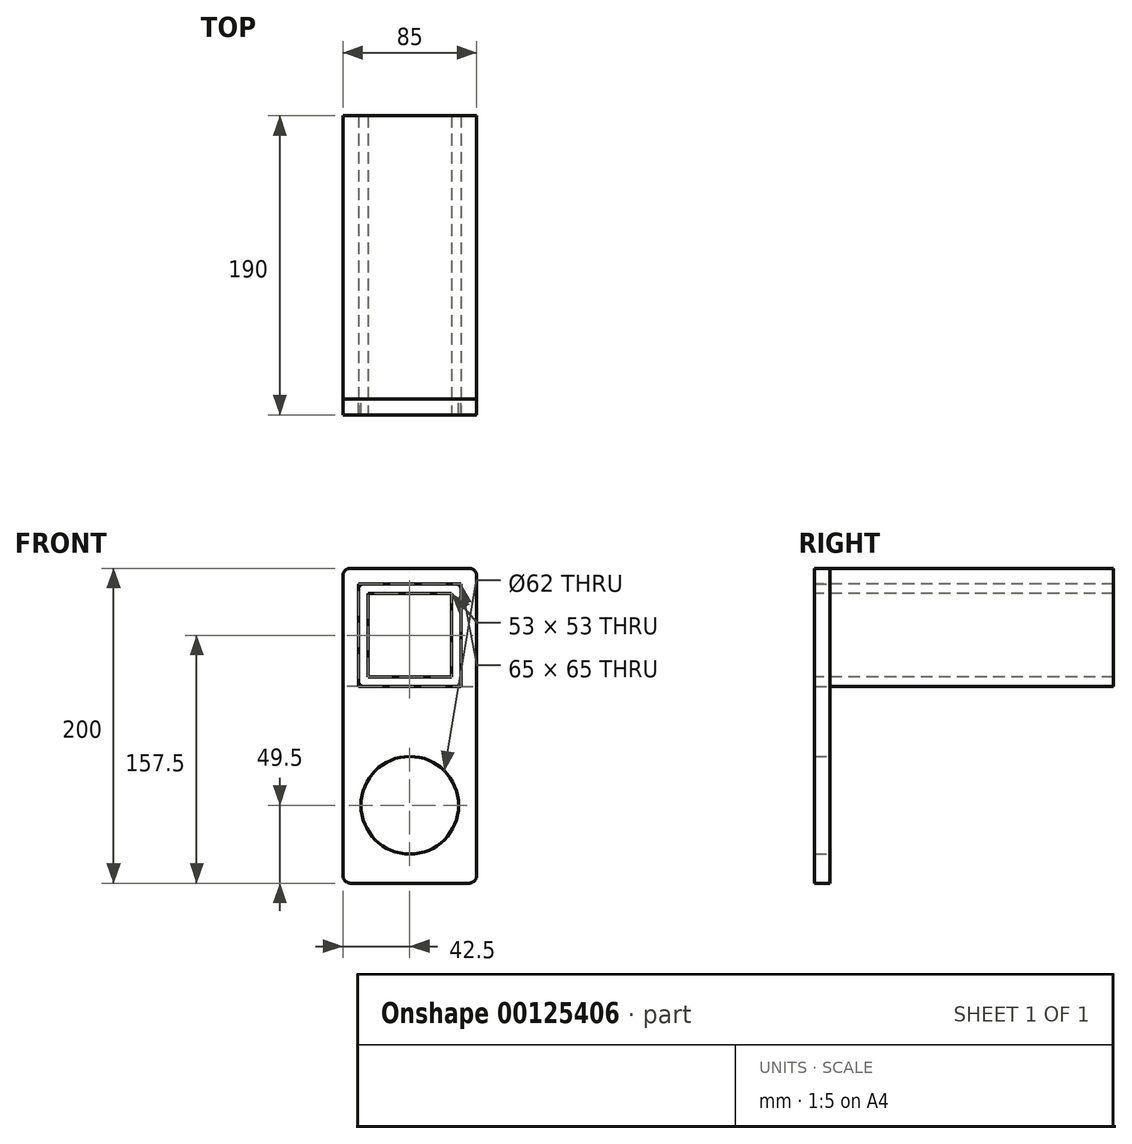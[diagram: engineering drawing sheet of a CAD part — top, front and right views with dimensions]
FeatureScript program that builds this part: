
annotation { "Feature Type Name" : "Feature", "Feature Type Description" : "" }
export const myFeature = defineFeature(function(context is Context, id is Id, definition is map)
    precondition{}
    {
        {
            var Q0;
            Q0=qCreatedBy(makeId("Front.planeOp"),FACE);
            var sketch = newSketch(context, id + "F0", { "sketchPlane" : qUnion([Q0])});
            skLineSegment(sketch, "E0", {"start": v(0, 0) * mm, "end": v(0, 125) * mm});
            skLineSegment(sketch, "E1", {"start": v(0, 0) * mm, "end": v(85, 0) * mm});
            skLineSegment(sketch, "E2", {"start": v(0, 125) * mm, "end": v(0, 200) * mm});
            skLineSegment(sketch, "E3", {"start": v(0, 200) * mm, "end": v(85, 200) * mm});
            skLineSegment(sketch, "E4", {"start": v(85, 200) * mm, "end": v(85, 0) * mm});
            skCircle(sketch, "E5", {"center": v(42.5, 49.5) * mm, "radius": 31 * mm});
            skLineSegment(sketch, "E6.bottom", {"start": v(10, 125) * mm, "end": v(75, 125) * mm});
            skLineSegment(sketch, "E6.top", {"start": v(10, 190) * mm, "end": v(75, 190) * mm});
            skLineSegment(sketch, "E6.left", {"start": v(10, 125) * mm, "end": v(10, 190) * mm});
            skLineSegment(sketch, "E6.right", {"start": v(75, 125) * mm, "end": v(75, 190) * mm});
            skSolve(sketch);
        }
        {
            var Q0;
            Q0 = qSketchRegion(id + "F0", true);
            var Q1;
            Q1=makeQuery(id+"F0.imprint","IMPRINT",FACE,{"disambiguationData":[TD([[makeQuery(id+"F0.imprint","IMPRINT",EDGE,{"derivedFrom":sQuery(id+"F0.wireOp",EDGE,"E0")}),-1.0]])]});
            extrude(context, id + "F1", {"entities" : qUnion([Q0, Q1]), "depth" : 10 * mm});
        }
        {
            var Q0;
            Q0=makeQuery(id+"F1.opExtrude","CAP_FACE",FACE,{"disambiguationData":[OSD([sQuery(id+"F0.wireOp",EDGE,"E0"),sQuery(id+"F0.wireOp",EDGE,"E1"),sQuery(id+"F0.wireOp",EDGE,"E2"),sQuery(id+"F0.wireOp",EDGE,"E3"),sQuery(id+"F0.wireOp",EDGE,"E4"),sQuery(id+"F0.wireOp",EDGE,"E5"),sQuery(id+"F0.wireOp",EDGE,"E6.bottom"),sQuery(id+"F0.wireOp",EDGE,"E6.top"),sQuery(id+"F0.wireOp",EDGE,"E6.left"),sQuery(id+"F0.wireOp",EDGE,"E6.right")])],"isStart":false});
            var sketch = newSketch(context, id + "F2", { "sketchPlane" : qUnion([Q0])});
            skLineSegment(sketch, "E7.bottom", {"start": v(13, 125) * mm, "end": v(72, 125) * mm});
            skLineSegment(sketch, "E7.top", {"start": v(13, 190) * mm, "end": v(72, 190) * mm});
            skLineSegment(sketch, "E7.left", {"start": v(10, 128) * mm, "end": v(10, 187) * mm});
            skLineSegment(sketch, "E7.right", {"start": v(75, 128) * mm, "end": v(75, 187) * mm});
            skPoint(sketch, "E8.visualSharp", {"position": v(10, 190) * mm});
            skArc(sketch, "E8.filletArc", {"start": v(13, 190) * mm, "mid": v(10.88, 189.12) * mm, "end": v(10, 187) * mm});
            skPoint(sketch, "E9.visualSharp", {"position": v(75, 190) * mm});
            skArc(sketch, "E9.filletArc", {"start": v(75, 187) * mm, "mid": v(74.12, 189.12) * mm, "end": v(72, 190) * mm});
            skPoint(sketch, "E10.visualSharp", {"position": v(75, 125) * mm});
            skArc(sketch, "E10.filletArc", {"start": v(72, 125) * mm, "mid": v(74.12, 125.88) * mm, "end": v(75, 128) * mm});
            skPoint(sketch, "E11.visualSharp", {"position": v(10, 125) * mm});
            skArc(sketch, "E11.filletArc", {"start": v(10, 128) * mm, "mid": v(10.88, 125.88) * mm, "end": v(13, 125) * mm});
            skLineSegment(sketch, "E12.0", {"start": v(16, 131) * mm, "end": v(69, 131) * mm});
            skLineSegment(sketch, "E12.1", {"start": v(16, 131) * mm, "end": v(16, 184) * mm});
            skLineSegment(sketch, "E12.2", {"start": v(16, 184) * mm, "end": v(69, 184) * mm});
            skLineSegment(sketch, "E12.3", {"start": v(69, 131) * mm, "end": v(69, 184) * mm});
            skSolve(sketch);
        }
        {
            var Q0;
            Q0=makeQuery(id+"F2.imprint","IMPRINT",FACE,{"disambiguationData":[TD([[makeQuery(id+"F2.imprint","IMPRINT",EDGE,{"derivedFrom":sQuery(id+"F2.wireOp",EDGE,"E7.bottom")}),1.0]])]});
            extrude(context, id + "F3", {"entities" : qUnion([Q0]), "oppositeDirection" : true, "depth" : 190 * mm});
        }
        {
            var Q0;
            Q0=makeQuery(id+"F1.opExtrude","CAP_FACE",FACE,{"disambiguationData":[OSD([sQuery(id+"F0.wireOp",EDGE,"E0"),sQuery(id+"F0.wireOp",EDGE,"E1"),sQuery(id+"F0.wireOp",EDGE,"E2"),sQuery(id+"F0.wireOp",EDGE,"E3"),sQuery(id+"F0.wireOp",EDGE,"E4"),sQuery(id+"F0.wireOp",EDGE,"E5"),sQuery(id+"F0.wireOp",EDGE,"E6.bottom"),sQuery(id+"F0.wireOp",EDGE,"E6.top"),sQuery(id+"F0.wireOp",EDGE,"E6.left"),sQuery(id+"F0.wireOp",EDGE,"E6.right")])],"isStart":true});
            var sketch = newSketch(context, id + "F4", { "sketchPlane" : qUnion([Q0])});
            skLineSegment(sketch, "E13", {"start": v(-75, 125) * mm, "end": v(-85, 125) * mm});
            skLineSegment(sketch, "E14", {"start": v(-10, 125) * mm, "end": v(0, 125) * mm});
            skLineSegment(sketch, "E15", {"start": v(0, 125) * mm, "end": v(0, 200) * mm});
            skLineSegment(sketch, "E16", {"start": v(0, 200) * mm, "end": v(-85, 200) * mm});
            skLineSegment(sketch, "E17", {"start": v(-85, 200) * mm, "end": v(-85, 125) * mm});
            skLineSegment(sketch, "E18", {"start": v(-75, 125) * mm, "end": v(-75, 190) * mm});
            skLineSegment(sketch, "E19", {"start": v(-75, 190) * mm, "end": v(-10, 190) * mm});
            skLineSegment(sketch, "E20", {"start": v(-10, 190) * mm, "end": v(-10, 125) * mm});
            skSolve(sketch);
        }
        {
            var Q0;
            Q0 = qSketchRegion(id + "F4", true);
            extrude(context, id + "F5", {"entities" : qUnion([Q0]), "depth" : 180 * mm});
        }
        {
            var Q0;
            Q0=makeQuery(id+"F5.opExtrude","SWEPT_EDGE",EDGE,{"disambiguationData":[OSD([sQuery(id+"F4.wireOp",EDGE,"E16"),sQuery(id+"F4.wireOp",EDGE,"E17")])]});
            var Q1;
            Q1=makeQuery(id+"F5.opExtrude","SWEPT_EDGE",EDGE,{"disambiguationData":[OSD([sQuery(id+"F4.wireOp",EDGE,"E15"),sQuery(id+"F4.wireOp",EDGE,"E16")])]});
            var Q2;
            Q2=makeQuery(id+"F1.opExtrude","SWEPT_EDGE",EDGE,{"disambiguationData":[OSD([sQuery(id+"F0.wireOp",EDGE,"E3"),sQuery(id+"F0.wireOp",EDGE,"E4")])]});
            var Q3;
            Q3=makeQuery(id+"F1.opExtrude","SWEPT_EDGE",EDGE,{"disambiguationData":[OSD([sQuery(id+"F0.wireOp",EDGE,"E2"),sQuery(id+"F0.wireOp",EDGE,"E3")])]});
            var Q4;
            Q4=makeQuery(id+"F1.opExtrude","SWEPT_EDGE",EDGE,{"disambiguationData":[OSD([sQuery(id+"F0.wireOp",EDGE,"E1"),sQuery(id+"F0.wireOp",EDGE,"E4")])]});
            var Q5;
            Q5=makeQuery(id+"F1.opExtrude","SWEPT_EDGE",EDGE,{"disambiguationData":[OSD([sQuery(id+"F0.wireOp",EDGE,"E0"),sQuery(id+"F0.wireOp",EDGE,"E1")])]});
            fillet(context, id + "F6", {"entities" : qUnion([Q0, Q1, Q2, Q3, Q4, Q5]), "radius" : 5 * mm, "tangentPropagation" : true, "allowEdgeOverflow" : false});
        }
    });
